# Revit family: 290413 ProLED SC combi ST LED 230V 1t_Vegg
name_source: partatom
category: Lighting Fixtures
revit_build: Autodesk Revit 2016 (Build: 20160314_0715(x64)
units: mm (PartAtom-declared; Revit-internal decimal feet)

## family parameters
Always vertical = Yes
Cut with Voids When Loaded = No
Light Source = Yes
OmniClass Number = 23.80.70.11.21
OmniClass Title = Emergency Lighting
Part Type = Normal
Room Calculation Point = No
Round Connector Dimension = Use Diameter
Shared = No
Work Plane-Based = No

## types (9) — shared parameters
Apparent Load = 17 VA
Body Material and Colour = Steel
Color Filter = 16777215
Dimming Lamp Color Temperature Shift = <None>
Emit Shape Visible in Rendering = No
Emit from Rectangle Length = 360 mm  [stored 1.1811 ft]
Emit from Rectangle Width = 145 mm  [stored 0.475722 ft]
Height = 145 mm  [stored 0.475722 ft]
Height 1 = 135 mm  [stored 0.442913 ft]
Keynote = WT2
Lamp = 1
Length = 360 mm  [stored 1.1811 ft]
Length 1 = 345 mm  [stored 1.13189 ft]
Manufacturer = Honeywell
Number of Poles = 1
Photometric Web File = 20x42A12.ies
Tilt Angle = 90.00°
Type Comments = -UN
Voltage = 230 V
Wattage Comments = 17 W
Width = 73 mm
zero-valued in all types: Height 2

## per-type parameters (varying)
| type | Assembly Code | LedeLys | ML | MarkeringsLys 45 Ned mot høyre | MarkeringsLys 45 Ned mot venstre | MarkeringsLys 45 Opp mot høyre | MarkeringsLys 45 Opp mot venstre | MarkeringsLys Høyre | MarkeringsLys Ned | MarkeringsLys Opp | MarkeringsLys Venstre | Markeringslys ikke normal | Markeringslys normal | NS8360 |
| LedeLys | 4432 | Yes | No | No | No | No | No | No | No | No | No | No | Yes | 4432_WT2 |
| MarkeringsLys (Ned) | 4431 | No | Yes | No | No | No | No | No | Yes | No | No | No | Yes | 4431_WT2 |
| MarkeringsLys (Opp) | 4431 | No | Yes | No | No | No | No | No | No | Yes | No | No | Yes | 4431_WT2 |
| MarkeringsLys (Venstre) | 4431 | No | Yes | No | No | No | No | No | No | No | Yes | Yes | No | 4431_WT2 |
| MarkeringsLys (Høyre) | 4431 | No | Yes | No | No | No | No | Yes | No | No | No | No | Yes | 4431_WT2 |
| MarkeringsLys (45 Ned mot høyre) | 4431 | No | Yes | Yes | No | No | No | No | No | No | No | No | Yes | 4431_WT2 |
| MarkeringsLys (45 Ned mot venstre) | 4431 | No | Yes | No | Yes | No | No | No | No | No | No | Yes | No | 4431_WT2 |
| MarkeringsLys (45 Opp mot høyre) | 4431 | No | Yes | No | No | Yes | No | No | No | No | No | No | Yes | 4431_WT2 |
| MarkeringsLys (45 Opp mot venstre) | 4431 | No | Yes | No | No | No | Yes | No | No | No | No | Yes | No | 4431_WT2 |

note: [stored X ft] marks values corroborated as IEEE doubles in the binary element streams (Revit-internal decimal feet)

## geometry (parser evidence)
native form markers: Sweep x29
no freeform markers — native parametric forms only
